# Revit family: Mailboxes_4C-Salsbury_Industries-Free_Standing-9_Door_High_Units
name_source: partatom
category: Specialty Equipment
revit_build: Autodesk Revit 2016 (Build: 20150714_1515(x64)
units: mm (PartAtom-declared; Revit-internal decimal feet)

## family parameters
Always vertical = Yes
Cut with Voids When Loaded = No
OmniClass Number = 23.40.90.14.11
OmniClass Title = Mail Boxes
Part Type = Normal
Room Calculation Point = No
Round Connector Dimension = Use Diameter
Shared = No
Work Plane-Based = No

## types (13) — shared parameters
4C Unit Elevation = 26.5 "
4C Unit Height = 34 "
Assembly Code = C1030910
Assembly Description = Mailboxes
Depth = 19 "
Front Panel Height = 25.504 "
Height = 62.25 "
Lock Material = Stainless Steel - Salsbury Finish -  Polished
Manufacturer = Salsbury Industries
MasterFormat Number = 10 55 00
MasterFormat Title = Postal Specialties
OmniClass 23 Number = 23.40.90.14.11
OmniClass 23 Title = Mail Boxes
Type Comments = Free-Standing 4C Horizontal Mailboxes - Front Loading
URL = www.mailboxes.com
Version = 1.0 (06/30/17)
Visible Door Number = Yes

## per-type parameters (varying)
| type | 4C Unit | Description | Width |
| 3909S-07 | Mailboxes_4C-Salsbury_Industries-Front_Load-9_Door_High_Units : 3709S-07 FL | 9 Door High Unit:  7 MB1, OM2 | 17.496 " |
| 3909D-16 | Mailboxes_4C-Salsbury_Industries-Front_Load-9_Door_High_Units : 3709D-16 FL | 9 Door High Unit:  16 MB1, OM2 | 32.25 " |
| 3909D-15 | Mailboxes_4C-Salsbury_Industries-Front_Load-9_Door_High_Units : 3709D-15 FL | 9 Door High Unit:  15 MB1, OM3 | 32.25 " |
| 3909D-10 | Mailboxes_4C-Salsbury_Industries-Front_Load-9_Door_High_Units : 3709D-10 FL | 9 Door High Unit:  10 MB1, 1 PL6, OM2 | 32.25 " |
| 3909D-06 | Mailboxes_4C-Salsbury_Industries-Front_Load-9_Door_High_Units : 3709D-06 FL | 9 Door High Unit:  1 MB1, 5 MB3, OM2 | 32.25 " |
| 3909D-05 | Mailboxes_4C-Salsbury_Industries-Front_Load-9_Door_High_Units : 3709D-05 FL | 9 Door High Unit:  5 MB3, OM3 | 32.25 " |
| 3909D-04 | Mailboxes_4C-Salsbury_Industries-Front_Load-9_Door_High_Units : 3709D-04 FL | 9 Door High Unit:  1 MB1, 3 MB3, 1 PL6, OM2 | 32.25 " |
| 3909D-03 | Mailboxes_4C-Salsbury_Industries-Front_Load-9_Door_High_Units : 3709D-03 FL | 9 Door High Unit:  3 MB3, 1 PL6, OM3 | 32.25 " |
| 3909D-4P | Mailboxes_4C-Salsbury_Industries-Front_Load-9_Door_High_Units : 3709D-4P FL | 9 Door High Unit:  2 PL4, 2 PL5 | 32.25 " |
| 3909S-02 | Mailboxes_4C-Salsbury_Industries-Front_Load-9_Door_High_Units : 3709S-02 FL | 9 Door High Unit:  2 MB1, 1 PL5, OM2 | 17.496 " |
| 3909S-2P | Mailboxes_4C-Salsbury_Industries-Front_Load-9_Door_High_Units : 3709S-2P FL | 9 Door High Unit:  1 PL4, 1 PL5 | 17.496 " |
| 3909S-1B | Mailboxes_4C-Salsbury_Industries-Front_Load-9_Door_High_Units : 3709S-1B FL | 9 Door High Unit:  1 Receptacle Bin | 17.496 " |
| 3909S-1C | Mailboxes_4C-Salsbury_Industries-Front_Load-9_Door_High_Units : 3709S-1C FL | 9 Door High Unit:  1 Collection Box | 17.496 " |

note: column(s) folded — value = type name in every type: Model

## geometry (parser evidence)
native form markers: Blend x6, Extrusion x4, Sweep x16
no freeform markers — native parametric forms only
